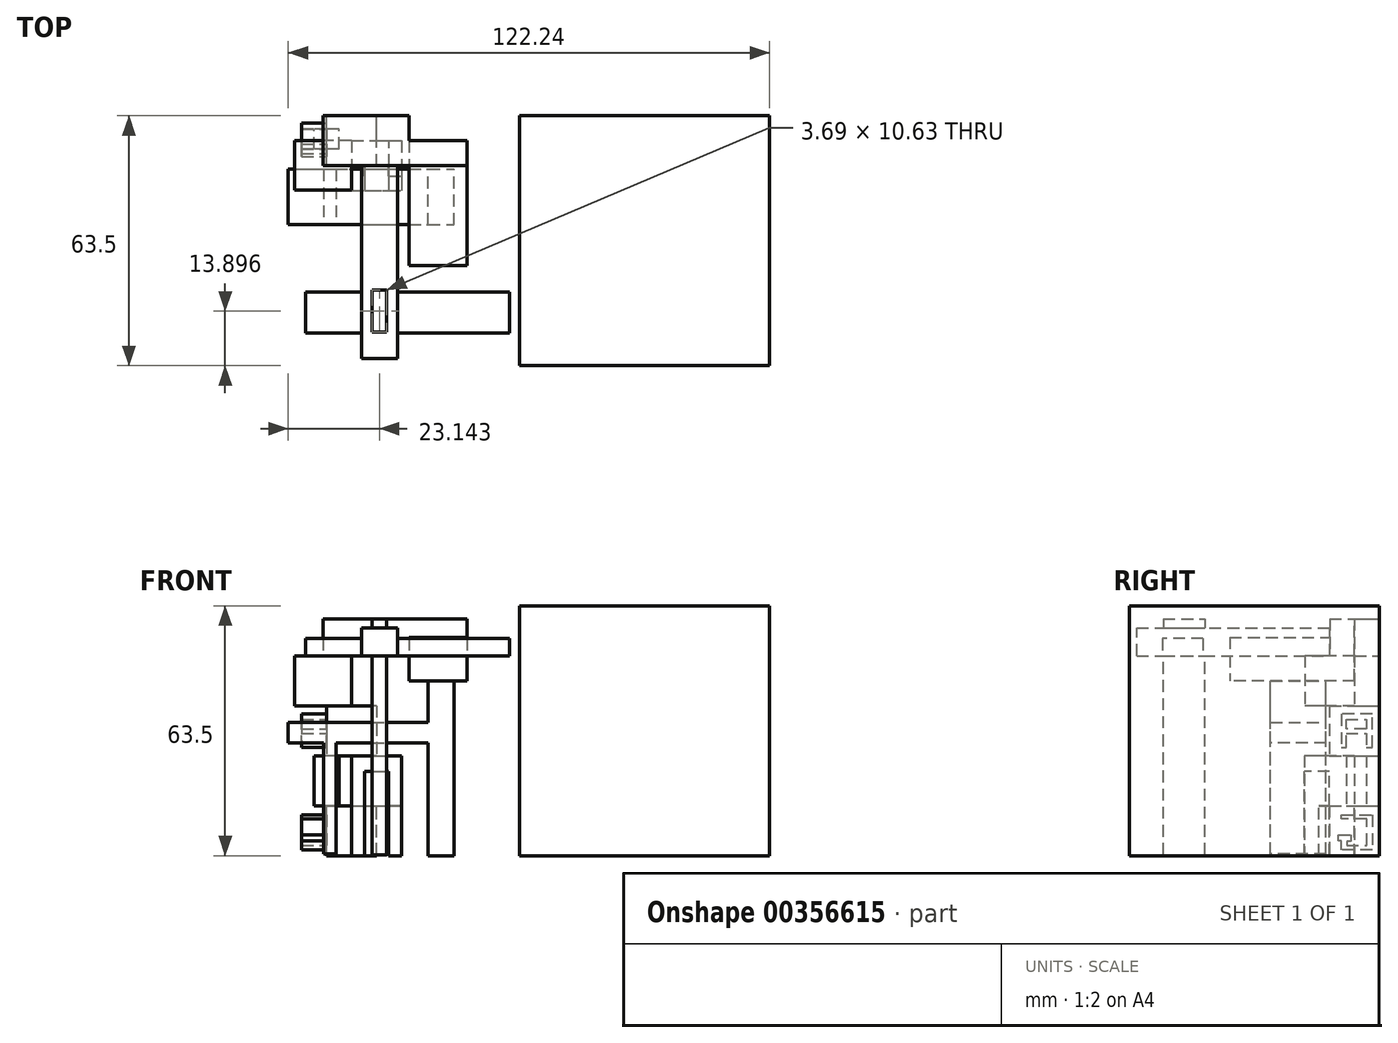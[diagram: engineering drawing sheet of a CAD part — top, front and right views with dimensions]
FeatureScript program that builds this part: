
annotation { "Feature Type Name" : "Feature", "Feature Type Description" : "" }
export const myFeature = defineFeature(function(context is Context, id is Id, definition is map)
    precondition{}
    {
        {
            var Q0;
            Q0=qCreatedBy(makeId("Front.planeOp"),FACE);
            var sketch = newSketch(context, id + "F0", { "sketchPlane" : qUnion([Q0])});
            skLineSegment(sketch, "E0.bottom", {"start": v(0, 0) * mm, "end": v(63.5, 0) * mm});
            skLineSegment(sketch, "E0.top", {"start": v(0, 63.5) * mm, "end": v(63.5, 63.5) * mm});
            skLineSegment(sketch, "E0.left", {"start": v(0, 0) * mm, "end": v(0, 63.5) * mm});
            skLineSegment(sketch, "E0.right", {"start": v(63.5, 0) * mm, "end": v(63.5, 63.5) * mm});
            skSolve(sketch);
        }
        {
            var Q0;
            Q0 = qSketchRegion(id + "F0", true);
            extrude(context, id + "F1", {"entities" : qUnion([Q0]), "depth" : 63.5 * mm});
        }
        {
            var Q0;
            Q0=qCreatedBy(makeId("Front.planeOp"),FACE);
            var sketch = newSketch(context, id + "F2", { "sketchPlane" : qUnion([Q0])});
            skLineSegment(sketch, "E1.bottom", {"start": v(-49.01, 0) * mm, "end": v(-36.31, 0) * mm});
            skLineSegment(sketch, "E1.top", {"start": v(-49.01, 12.7) * mm, "end": v(-36.31, 12.7) * mm});
            skLineSegment(sketch, "E1.left", {"start": v(-49.01, 0) * mm, "end": v(-49.01, 12.7) * mm});
            skLineSegment(sketch, "E1.right", {"start": v(-36.31, 0) * mm, "end": v(-36.31, 12.7) * mm});
            skSolve(sketch);
        }
        {
            var Q0;
            Q0 = qSketchRegion(id + "F2", true);
            extrude(context, id + "F3", {"entities" : qUnion([Q0]), "depth" : 12.7 * mm});
        }
        {
            var Q0;
            Q0=makeQuery(id+"F3.opExtrude","SWEPT_FACE",FACE,{"disambiguationData":[OSD([sQuery(id+"F2.wireOp",EDGE,"E1.top")])]});
            var sketch = newSketch(context, id + "F4", { "sketchPlane" : qUnion([Q0])});
            skPoint(sketch, "E2.firstSnap0", {"position": v(-36.31, -6.35) * mm});
            skPoint(sketch, "E2.firstSnap1", {"position": v(-42.66, -12.7) * mm});
            skLineSegment(sketch, "E2.bottom", {"start": v(-42.66, -6.35) * mm, "end": v(-29.96, -6.35) * mm});
            skLineSegment(sketch, "E2.top", {"start": v(-42.66, -19.05) * mm, "end": v(-29.96, -19.05) * mm});
            skLineSegment(sketch, "E2.left", {"start": v(-42.66, -6.35) * mm, "end": v(-42.66, -19.05) * mm});
            skLineSegment(sketch, "E2.right", {"start": v(-29.96, -6.35) * mm, "end": v(-29.96, -19.05) * mm});
            skSolve(sketch);
        }
        {
            var Q0;
            {var subQ0=sQuery(id+"F4.wireOp",EDGE,"E2.left");var subQ1=sQuery(id+"F4.wireOp",EDGE,"E2.bottom");var subQ2=makeQuery(id+"F4.imprint","INTERSECT",VERTEX,{"derivedFrom":[subQ1,subQ0]});Q0=makeQuery(id+"F4.imprint","IMPRINT",FACE,{"disambiguationData":[TD([[makeQuery(id+"F4.imprint","IMPRINT",EDGE,{"disambiguationData":[TD([[subQ2,-1.0]])],"derivedFrom":subQ0}),1.0]])]});}
            var Q1;
            {var subQ2=sQuery(id+"F4.wireOp",EDGE,"E2.top");Q1=makeQuery(id+"F4.imprint","IMPRINT",FACE,{"disambiguationData":[TD([[makeQuery(id+"F4.imprint","IMPRINT",EDGE,{"derivedFrom":subQ2}),1.0]])]});}
            extrude(context, id + "F5", {"entities" : qUnion([Q0, Q1]), "operationType" : NewBodyOperationType.ADD, "depth" : 12.7 * mm});
        }
        {
            var Q0;
            Q0=makeQuery(id+"F5.opExtrude","CAP_FACE",FACE,{"disambiguationData":[OSD([sQuery(id+"F4.wireOp",EDGE,"E2.bottom"),sQuery(id+"F4.wireOp",EDGE,"E2.top"),sQuery(id+"F4.wireOp",EDGE,"E2.left"),sQuery(id+"F4.wireOp",EDGE,"E2.right")])],"isStart":false});
            var sketch = newSketch(context, id + "F6", { "sketchPlane" : qUnion([Q0])});
            skPoint(sketch, "E3.firstSnap0", {"position": v(-42.66, -12.7) * mm});
            skPoint(sketch, "E3.firstSnap1", {"position": v(-36.31, -6.35) * mm});
            skLineSegment(sketch, "E3.bottom", {"start": v(-36.31, -12.7) * mm, "end": v(-49.01, -12.7) * mm});
            skLineSegment(sketch, "E3.top", {"start": v(-36.31, 0) * mm, "end": v(-49.01, 0) * mm});
            skLineSegment(sketch, "E3.left", {"start": v(-36.31, -12.7) * mm, "end": v(-36.31, 0) * mm});
            skLineSegment(sketch, "E3.right", {"start": v(-49.01, -12.7) * mm, "end": v(-49.01, 0) * mm});
            skSolve(sketch);
        }
        {
            var Q0;
            Q0 = qSketchRegion(id + "F6", true);
            extrude(context, id + "F7", {"entities" : qUnion([Q0]), "operationType" : NewBodyOperationType.ADD, "depth" : 12.7 * mm});
        }
        {
            var Q0;
            Q0=makeQuery(id+"F3.opExtrude","SWEPT_FACE",FACE,{"disambiguationData":[OSD([sQuery(id+"F2.wireOp",EDGE,"E1.top")])]});
            var sketch = newSketch(context, id + "F8", { "sketchPlane" : qUnion([Q0])});
            skPoint(sketch, "E4.firstSnap0", {"position": v(-45.84, -12.7) * mm});
            skLineSegment(sketch, "E4.bottom", {"start": v(-45.84, -8.44) * mm, "end": v(-52.2, -8.44) * mm});
            skLineSegment(sketch, "E4.top", {"start": v(-45.84, -3.37) * mm, "end": v(-52.2, -3.37) * mm});
            skLineSegment(sketch, "E4.left", {"start": v(-45.84, -8.44) * mm, "end": v(-45.84, -3.37) * mm});
            skLineSegment(sketch, "E4.right", {"start": v(-52.2, -8.44) * mm, "end": v(-52.2, -3.37) * mm});
            skSolve(sketch);
        }
        {
            var Q0;
            Q0 = qSketchRegion(id + "F8", true);
            extrude(context, id + "F9", {"entities" : qUnion([Q0]), "operationType" : NewBodyOperationType.ADD, "depth" : 12.7 * mm});
        }
        {
            var Q0;
            Q0=makeQuery(id+"F5.opExtrude","CAP_FACE",FACE,{"disambiguationData":[OSD([sQuery(id+"F4.wireOp",EDGE,"E2.bottom"),sQuery(id+"F4.wireOp",EDGE,"E2.top"),sQuery(id+"F4.wireOp",EDGE,"E2.left"),sQuery(id+"F4.wireOp",EDGE,"E2.right")])],"isStart":true});
            var sketch = newSketch(context, id + "F10", { "sketchPlane" : qUnion([Q0])});
            skLineSegment(sketch, "E5", {"start": v(-39.49, 12.7) * mm, "end": v(-39.49, 15.34) * mm});
            skLineSegment(sketch, "E6", {"start": v(-39.49, 15.34) * mm, "end": v(-33.14, 15.34) * mm});
            skPoint(sketch, "E6.endSnap0", {"position": v(-33.14, 6.35) * mm});
            skLineSegment(sketch, "E7", {"start": v(-33.14, 15.34) * mm, "end": v(-33.14, 6.35) * mm});
            skSolve(sketch);
        }
        {
            var Q0;
            Q0 = qSketchRegion(id + "F10", true);
            var Q1;
            {var subQ2=sQuery(id+"F10.wireOp",EDGE,"E5");Q1=makeQuery(id+"F10.imprint","IMPRINT",FACE,{"disambiguationData":[TD([[makeQuery(id+"F10.imprint","IMPRINT",EDGE,{"derivedFrom":subQ2}),1.0]])]});}
            extrude(context, id + "F11", {"entities" : qUnion([Q0, Q1]), "operationType" : NewBodyOperationType.ADD, "depth" : 12.7 * mm});
        }
        {
            var Q0;
            {var subQ0=sQuery(id+"F4.wireOp",EDGE,"E2.top");Q0=makeQuery(id+"F11.boolean.opBoolean","MERGE",FACE,{"derivedFrom":[makeQuery(id+"F5.opExtrude","SWEPT_FACE",FACE,{"disambiguationData":[OSD([subQ0])]}),makeQuery(id+"F11.opExtrude","SWEPT_FACE",FACE,{"disambiguationData":[OSD([subQ0])]})]});}
            var sketch = newSketch(context, id + "F12", { "sketchPlane" : qUnion([Q0])});
            skLineSegment(sketch, "E8.bottom", {"start": v(-39.34, 0) * mm, "end": v(-33.22, 0) * mm});
            skLineSegment(sketch, "E8.top", {"start": v(-39.34, 21.42) * mm, "end": v(-33.22, 21.42) * mm});
            skLineSegment(sketch, "E8.left", {"start": v(-39.34, 0) * mm, "end": v(-39.34, 21.42) * mm});
            skLineSegment(sketch, "E8.right", {"start": v(-33.22, 0) * mm, "end": v(-33.22, 21.42) * mm});
            skSolve(sketch);
        }
        {
            var Q0;
            Q0 = qSketchRegion(id + "F12", true);
            extrude(context, id + "F13", {"entities" : qUnion([Q0]), "operationType" : NewBodyOperationType.REMOVE, "oppositeDirection" : true, "depth" : 6.35 * mm});
        }
        {
            var Q0;
            Q0=makeQuery(id+"F11.opExtrude","SWEPT_FACE",FACE,{"disambiguationData":[OSD([sQuery(id+"F10.wireOp",EDGE,"E7")])]});
            var sketch = newSketch(context, id + "F14", { "sketchPlane" : qUnion([Q0])});
            skLineSegment(sketch, "E9", {"start": v(12.75, 12.7) * mm, "end": v(12.75, 0) * mm});
            skSolve(sketch);
        }
        {
            var Q0;
            {var subQ0=sQuery(id+"F14.wireOp",EDGE,"E9");Q0=makeQuery(id+"F14.imprint","IMPRINT",FACE,{"disambiguationData":[TD([[makeQuery(id+"F14.imprint","IMPRINT",EDGE,{"derivedFrom":subQ0}),1.0]])]});}
            extrude(context, id + "F15", {"entities" : qUnion([Q0]), "operationType" : NewBodyOperationType.REMOVE, "oppositeDirection" : true, "depth" : 6.35 * mm});
        }
        {
            var Q0;
            Q0=makeQuery(id+"F7.opExtrude","CAP_FACE",FACE,{"disambiguationData":[OSD([sQuery(id+"F6.wireOp",EDGE,"E3.bottom"),sQuery(id+"F6.wireOp",EDGE,"E3.top"),sQuery(id+"F6.wireOp",EDGE,"E3.left"),sQuery(id+"F6.wireOp",EDGE,"E3.right")])],"isStart":false});
            var sketch = newSketch(context, id + "F16", { "sketchPlane" : qUnion([Q0])});
            skPoint(sketch, "E10.firstSnap0", {"position": v(-42.66, -12.7) * mm});
            skPoint(sketch, "E10.firstSnap1", {"position": v(-36.31, -6.35) * mm});
            skLineSegment(sketch, "E10.bottom", {"start": v(-42.66, -6.35) * mm, "end": v(-57.1, -6.35) * mm});
            skLineSegment(sketch, "E10.top", {"start": v(-42.66, -18.9) * mm, "end": v(-57.1, -18.9) * mm});
            skLineSegment(sketch, "E10.left", {"start": v(-42.66, -6.35) * mm, "end": v(-42.66, -18.9) * mm});
            skLineSegment(sketch, "E10.right", {"start": v(-57.1, -6.35) * mm, "end": v(-57.1, -18.9) * mm});
            skSolve(sketch);
        }
        {
            var Q0;
            Q0 = qSketchRegion(id + "F16", true);
            extrude(context, id + "F17", {"entities" : qUnion([Q0]), "operationType" : NewBodyOperationType.ADD, "depth" : 12.7 * mm});
        }
        {
            var Q0;
            Q0=makeQuery(id+"F17.opExtrude","CAP_FACE",FACE,{"disambiguationData":[OSD([sQuery(id+"F16.wireOp",EDGE,"E10.bottom"),sQuery(id+"F16.wireOp",EDGE,"E10.top"),sQuery(id+"F16.wireOp",EDGE,"E10.left"),sQuery(id+"F16.wireOp",EDGE,"E10.right")])],"isStart":false});
            var sketch = newSketch(context, id + "F18", { "sketchPlane" : qUnion([Q0])});
            skPoint(sketch, "E11.firstSnap0", {"position": v(-49.88, -6.35) * mm});
            skPoint(sketch, "E11.firstSnap1", {"position": v(-57.1, -12.62) * mm});
            skLineSegment(sketch, "E11.bottom", {"start": v(-49.88, -12.62) * mm, "end": v(-13.34, -12.62) * mm});
            skLineSegment(sketch, "E11.top", {"start": v(-49.88, 0) * mm, "end": v(-13.34, 0) * mm});
            skLineSegment(sketch, "E11.left", {"start": v(-49.88, -12.62) * mm, "end": v(-49.88, 0) * mm});
            skLineSegment(sketch, "E11.right", {"start": v(-13.34, -12.62) * mm, "end": v(-13.34, 0) * mm});
            skSolve(sketch);
        }
        {
            var Q0;
            Q0 = qSketchRegion(id + "F18", true);
            extrude(context, id + "F19", {"entities" : qUnion([Q0]), "operationType" : NewBodyOperationType.ADD, "depth" : 9.4 * mm});
        }
        {
            var Q0;
            Q0=makeQuery(id+"F19.opExtrude","SWEPT_FACE",FACE,{"disambiguationData":[OSD([sQuery(id+"F18.wireOp",EDGE,"E11.bottom")])]});
            var sketch = newSketch(context, id + "F20", { "sketchPlane" : qUnion([Q0])});
            skPoint(sketch, "E12.firstSnap0", {"position": v(-13.34, 55.5) * mm});
            skPoint(sketch, "E12.firstSnap1", {"position": v(-28, 50.8) * mm});
            skLineSegment(sketch, "E12.bottom", {"start": v(-28, 55.5) * mm, "end": v(-13.34, 55.5) * mm});
            skLineSegment(sketch, "E12.top", {"start": v(-28, 50.8) * mm, "end": v(-13.34, 50.8) * mm});
            skLineSegment(sketch, "E12.left", {"start": v(-28, 55.5) * mm, "end": v(-28, 50.8) * mm});
            skLineSegment(sketch, "E12.right", {"start": v(-13.34, 55.5) * mm, "end": v(-13.34, 50.8) * mm});
            skSolve(sketch);
        }
        {
            var Q0;
            Q0 = qSketchRegion(id + "F20", true);
            extrude(context, id + "F21", {"entities" : qUnion([Q0]), "operationType" : NewBodyOperationType.ADD, "depth" : 25.4 * mm});
        }
        {
            var Q0;
            Q0=makeQuery(id+"F21.boolean.opBoolean","MERGE",FACE,{"derivedFrom":[makeQuery(id+"F19.opExtrude","CAP_FACE",FACE,{"disambiguationData":[OSD([sQuery(id+"F18.wireOp",EDGE,"E11.bottom"),sQuery(id+"F18.wireOp",EDGE,"E11.top"),sQuery(id+"F18.wireOp",EDGE,"E11.left"),sQuery(id+"F18.wireOp",EDGE,"E11.right")])],"isStart":true}),makeQuery(id+"F21.opExtrude","SWEPT_FACE",FACE,{"disambiguationData":[OSD([sQuery(id+"F20.wireOp",EDGE,"E12.top")])]})]});
            var sketch = newSketch(context, id + "F22", { "sketchPlane" : qUnion([Q0])});
            skLineSegment(sketch, "E13.bottom", {"start": v(-13.34, 0) * mm, "end": v(-28, 0) * mm});
            skLineSegment(sketch, "E13.top", {"start": v(-13.34, 38.02) * mm, "end": v(-28, 38.02) * mm});
            skLineSegment(sketch, "E13.left", {"start": v(-13.34, 0) * mm, "end": v(-13.34, 38.02) * mm});
            skLineSegment(sketch, "E13.right", {"start": v(-28, 0) * mm, "end": v(-28, 38.02) * mm});
            skSolve(sketch);
        }
        {
            var Q0;
            Q0 = qSketchRegion(id + "F22", true);
            extrude(context, id + "F23", {"entities" : qUnion([Q0]), "operationType" : NewBodyOperationType.ADD, "depth" : 6.35 * mm});
        }
        {
            var Q0;
            Q0=makeQuery(id+"F23.boolean.opBoolean","MERGE",FACE,{"derivedFrom":[makeQuery(id+"F19.opExtrude","SWEPT_FACE",FACE,{"disambiguationData":[OSD([sQuery(id+"F18.wireOp",EDGE,"E11.top")])]}),makeQuery(id+"F23.opExtrude","SWEPT_FACE",FACE,{"disambiguationData":[OSD([sQuery(id+"F22.wireOp",EDGE,"E13.bottom")])]})]});
            var sketch = newSketch(context, id + "F24", { "sketchPlane" : qUnion([Q0])});
            skLineSegment(sketch, "E14.bottom", {"start": v(13.34, 44.45) * mm, "end": v(28, 44.45) * mm});
            skLineSegment(sketch, "E14.top", {"start": v(13.34, 60.2) * mm, "end": v(28, 60.2) * mm});
            skLineSegment(sketch, "E14.left", {"start": v(13.34, 44.45) * mm, "end": v(13.34, 60.2) * mm});
            skLineSegment(sketch, "E14.right", {"start": v(28, 44.45) * mm, "end": v(28, 60.2) * mm});
            skSolve(sketch);
        }
        {
            var Q0;
            Q0 = qSketchRegion(id + "F24", true);
            extrude(context, id + "F25", {"entities" : qUnion([Q0]), "operationType" : NewBodyOperationType.REMOVE, "oppositeDirection" : true, "depth" : 6.35 * mm});
        }
        {
            var Q0;
            Q0=makeQuery(id+"F23.opExtrude","CAP_FACE",FACE,{"disambiguationData":[OSD([sQuery(id+"F22.wireOp",EDGE,"E13.bottom"),sQuery(id+"F22.wireOp",EDGE,"E13.top"),sQuery(id+"F22.wireOp",EDGE,"E13.left"),sQuery(id+"F22.wireOp",EDGE,"E13.right")])],"isStart":false});
            var sketch = newSketch(context, id + "F26", { "sketchPlane" : qUnion([Q0])});
            skLineSegment(sketch, "E15.bottom", {"start": v(-23.18, 27.66) * mm, "end": v(-16.66, 27.66) * mm});
            skLineSegment(sketch, "E15.top", {"start": v(-23.18, 13.6) * mm, "end": v(-16.66, 13.6) * mm});
            skLineSegment(sketch, "E15.left", {"start": v(-23.18, 27.66) * mm, "end": v(-23.18, 13.6) * mm});
            skLineSegment(sketch, "E15.right", {"start": v(-16.66, 27.66) * mm, "end": v(-16.66, 13.6) * mm});
            skSolve(sketch);
        }
        {
            var Q0;
            Q0 = qSketchRegion(id + "F26", true);
            extrude(context, id + "F27", {"entities" : qUnion([Q0]), "operationType" : NewBodyOperationType.ADD, "depth" : 44.45 * mm});
        }
        {
            var Q0;
            Q0=makeQuery(id+"F27.opExtrude","SWEPT_FACE",FACE,{"disambiguationData":[OSD([sQuery(id+"F26.wireOp",EDGE,"E15.left")])]});
            var sketch = newSketch(context, id + "F28", { "sketchPlane" : qUnion([Q0])});
            skLineSegment(sketch, "E16.bottom", {"start": v(27.66, 33.87) * mm, "end": v(13.6, 33.87) * mm});
            skLineSegment(sketch, "E16.top", {"start": v(27.66, 28.6) * mm, "end": v(13.6, 28.6) * mm});
            skLineSegment(sketch, "E16.left", {"start": v(27.66, 33.87) * mm, "end": v(27.66, 28.6) * mm});
            skLineSegment(sketch, "E16.right", {"start": v(13.6, 33.87) * mm, "end": v(13.6, 28.6) * mm});
            skSolve(sketch);
        }
        {
            var Q0;
            Q0 = qSketchRegion(id + "F28", true);
            extrude(context, id + "F29", {"entities" : qUnion([Q0]), "operationType" : NewBodyOperationType.ADD, "depth" : 35.56 * mm});
        }
        {
            var Q0;
            Q0=makeQuery(id+"F29.opExtrude","SWEPT_FACE",FACE,{"disambiguationData":[OSD([sQuery(id+"F28.wireOp",EDGE,"E16.top")])]});
            var sketch = newSketch(context, id + "F30", { "sketchPlane" : qUnion([Q0])});
            skLineSegment(sketch, "E17.bottom", {"start": v(-49.78, 13.6) * mm, "end": v(-46.63, 13.6) * mm});
            skLineSegment(sketch, "E17.top", {"start": v(-49.78, 27.66) * mm, "end": v(-46.63, 27.66) * mm});
            skLineSegment(sketch, "E17.left", {"start": v(-49.78, 13.6) * mm, "end": v(-49.78, 27.66) * mm});
            skLineSegment(sketch, "E17.right", {"start": v(-46.63, 13.6) * mm, "end": v(-46.63, 27.66) * mm});
            skSolve(sketch);
        }
        {
            var Q0;
            Q0 = qSketchRegion(id + "F30", true);
            extrude(context, id + "F31", {"entities" : qUnion([Q0]), "operationType" : NewBodyOperationType.ADD, "depth" : 28.2 * mm});
        }
        {
            var Q0;
            Q0=makeQuery(id+"F19.opExtrude","SWEPT_FACE",FACE,{"disambiguationData":[OSD([sQuery(id+"F18.wireOp",EDGE,"E11.bottom")])]});
            var sketch = newSketch(context, id + "F32", { "sketchPlane" : qUnion([Q0])});
            skLineSegment(sketch, "E18.bottom", {"start": v(-40.13, 50.8) * mm, "end": v(-30.98, 50.8) * mm});
            skLineSegment(sketch, "E18.top", {"start": v(-40.13, 57.88) * mm, "end": v(-30.98, 57.88) * mm});
            skLineSegment(sketch, "E18.left", {"start": v(-40.13, 50.8) * mm, "end": v(-40.13, 57.88) * mm});
            skLineSegment(sketch, "E18.right", {"start": v(-30.98, 50.8) * mm, "end": v(-30.98, 57.88) * mm});
            skSolve(sketch);
        }
        {
            var Q0;
            Q0 = qSketchRegion(id + "F32", true);
            extrude(context, id + "F33", {"entities" : qUnion([Q0]), "operationType" : NewBodyOperationType.ADD, "depth" : 49.02 * mm});
        }
        {
            var Q0;
            Q0=makeQuery(id+"F33.opExtrude","SWEPT_FACE",FACE,{"disambiguationData":[OSD([sQuery(id+"F32.wireOp",EDGE,"E18.right")])]});
            var sketch = newSketch(context, id + "F34", { "sketchPlane" : qUnion([Q0])});
            skLineSegment(sketch, "E19.bottom", {"start": v(-55.18, 50.8) * mm, "end": v(-44.81, 50.8) * mm});
            skLineSegment(sketch, "E19.top", {"start": v(-55.18, 55.15) * mm, "end": v(-44.81, 55.15) * mm});
            skLineSegment(sketch, "E19.left", {"start": v(-55.18, 50.8) * mm, "end": v(-55.18, 55.15) * mm});
            skLineSegment(sketch, "E19.right", {"start": v(-44.81, 50.8) * mm, "end": v(-44.81, 55.15) * mm});
            skSolve(sketch);
        }
        {
            var Q0;
            Q0 = qSketchRegion(id + "F34", true);
            extrude(context, id + "F35", {"entities" : qUnion([Q0]), "operationType" : NewBodyOperationType.ADD, "depth" : 28.45 * mm});
        }
        {
            var Q0;
            Q0 = qSketchRegion(id + "F34", true);
            extrude(context, id + "F36", {"entities" : qUnion([Q0]), "operationType" : NewBodyOperationType.ADD, "oppositeDirection" : true, "depth" : 23.37 * mm});
        }
        {
            var Q0;
            Q0=makeQuery(id+"F33.opExtrude","SWEPT_FACE",FACE,{"disambiguationData":[OSD([sQuery(id+"F32.wireOp",EDGE,"E18.top")])]});
            var sketch = newSketch(context, id + "F37", { "sketchPlane" : qUnion([Q0])});
            skLineSegment(sketch, "E20.bottom", {"start": v(-37.44, -54.92) * mm, "end": v(-33.75, -54.92) * mm});
            skLineSegment(sketch, "E20.top", {"start": v(-37.44, -44.29) * mm, "end": v(-33.75, -44.29) * mm});
            skLineSegment(sketch, "E20.left", {"start": v(-37.44, -54.92) * mm, "end": v(-37.44, -44.29) * mm});
            skLineSegment(sketch, "E20.right", {"start": v(-33.75, -54.92) * mm, "end": v(-33.75, -44.29) * mm});
            skSolve(sketch);
        }
        {
            var Q0;
            Q0 = qSketchRegion(id + "F37", true);
            extrude(context, id + "F38", {"entities" : qUnion([Q0]), "operationType" : NewBodyOperationType.ADD, "depth" : 2.3 * mm});
        }
        {
            var Q0;
            Q0 = qSketchRegion(id + "F37", true);
            extrude(context, id + "F39", {"entities" : qUnion([Q0]), "operationType" : NewBodyOperationType.ADD, "oppositeDirection" : true, "depth" : 57.66 * mm});
        }
        {
            var Q0;
            Q0=makeQuery(id+"F7.opExtrude","SWEPT_FACE",FACE,{"disambiguationData":[OSD([sQuery(id+"F6.wireOp",EDGE,"E3.right")])]});
            var sketch = newSketch(context, id + "F40", { "sketchPlane" : qUnion([Q0])});
            skLineSegment(sketch, "E21", {"start": v(1.8, 27.54) * mm, "end": v(1.8, 35.98) * mm});
            skLineSegment(sketch, "E22", {"start": v(1.8, 35.98) * mm, "end": v(9.65, 35.98) * mm});
            skLineSegment(sketch, "E23", {"start": v(9.65, 35.98) * mm, "end": v(9.65, 27.54) * mm});
            skLineSegment(sketch, "E24", {"start": v(9.65, 27.54) * mm, "end": v(8.44, 27.54) * mm});
            skLineSegment(sketch, "E25", {"start": v(8.44, 27.54) * mm, "end": v(8.44, 34.66) * mm});
            skLineSegment(sketch, "E26", {"start": v(8.44, 34.66) * mm, "end": v(3.37, 34.66) * mm});
            skLineSegment(sketch, "E27", {"start": v(3.37, 34.66) * mm, "end": v(3.37, 27.54) * mm});
            skLineSegment(sketch, "E28", {"start": v(3.37, 27.54) * mm, "end": v(1.8, 27.54) * mm});
            skLineSegment(sketch, "E29", {"start": v(3.37, 32.25) * mm, "end": v(8.44, 32.25) * mm});
            skLineSegment(sketch, "E30", {"start": v(8.44, 32.25) * mm, "end": v(8.44, 31.1) * mm});
            skLineSegment(sketch, "E31", {"start": v(8.44, 31.1) * mm, "end": v(3.37, 31.1) * mm});
            skLineSegment(sketch, "E32", {"start": v(3.37, 31.1) * mm, "end": v(3.37, 32.25) * mm});
            skLineSegment(sketch, "E33", {"start": v(9.65, 10.32) * mm, "end": v(1.8, 10.32) * mm});
            skLineSegment(sketch, "E34", {"start": v(1.8, 10.32) * mm, "end": v(1.8, 1.52) * mm});
            skLineSegment(sketch, "E35", {"start": v(1.8, 1.52) * mm, "end": v(9.65, 1.52) * mm});
            skLineSegment(sketch, "E36", {"start": v(9.65, 1.52) * mm, "end": v(9.65, 3.76) * mm});
            skLineSegment(sketch, "E37", {"start": v(9.65, 3.76) * mm, "end": v(10.4, 3.76) * mm});
            skLineSegment(sketch, "E38", {"start": v(10.4, 3.76) * mm, "end": v(10.4, 5.26) * mm});
            skLineSegment(sketch, "E39", {"start": v(10.4, 5.26) * mm, "end": v(7.24, 5.26) * mm});
            skLineSegment(sketch, "E40", {"start": v(7.24, 5.26) * mm, "end": v(7.24, 3.6) * mm});
            skLineSegment(sketch, "E41", {"start": v(7.24, 3.6) * mm, "end": v(8.32, 3.6) * mm});
            skLineSegment(sketch, "E42", {"start": v(8.32, 3.6) * mm, "end": v(8.32, 2.68) * mm});
            skLineSegment(sketch, "E43", {"start": v(8.32, 2.68) * mm, "end": v(3.26, 2.68) * mm});
            skLineSegment(sketch, "E44", {"start": v(3.26, 2.68) * mm, "end": v(3.26, 9.33) * mm});
            skLineSegment(sketch, "E45", {"start": v(3.26, 9.33) * mm, "end": v(9.65, 9.33) * mm});
            skLineSegment(sketch, "E46", {"start": v(9.65, 9.33) * mm, "end": v(9.65, 10.32) * mm});
            skSolve(sketch);
        }
        {
            var Q0;
            Q0 = qSketchRegion(id + "F40", true);
            extrude(context, id + "F41", {"entities" : qUnion([Q0]), "operationType" : NewBodyOperationType.ADD, "depth" : 6.35 * mm});
        }
    });
